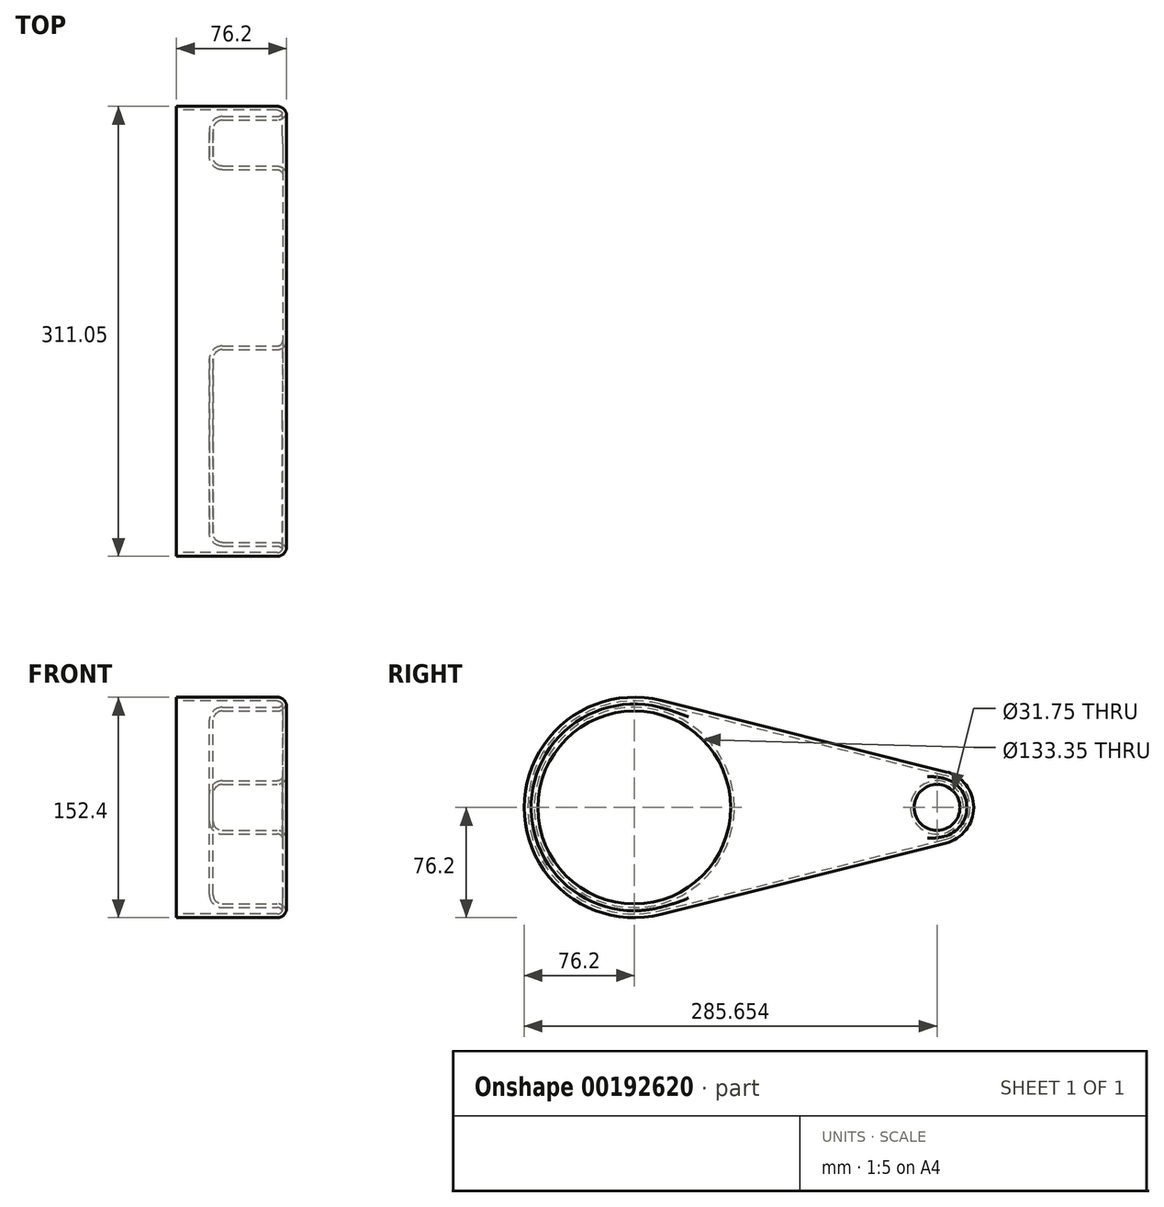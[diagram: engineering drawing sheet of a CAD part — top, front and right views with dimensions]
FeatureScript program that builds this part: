
annotation { "Feature Type Name" : "Feature", "Feature Type Description" : "" }
export const myFeature = defineFeature(function(context is Context, id is Id, definition is map)
    precondition{}
    {
        {
            var Q0;
            Q0=qCreatedBy(makeId("Right.planeOp"),FACE);
            var sketch = newSketch(context, id + "F0", { "sketchPlane" : qUnion([Q0])});
            skCircle(sketch, "E0", {"center": v(0, 0) * mm, "radius": 76.2 * mm});
            skCircle(sketch, "E1", {"center": v(209.45, 0) * mm, "radius": 25.4 * mm});
            skLineSegment(sketch, "E2", {"start": v(18.48, 73.92) * mm, "end": v(215.61, 24.64) * mm});
            skLineSegment(sketch, "E3", {"start": v(18.48, -73.92) * mm, "end": v(215.61, -24.64) * mm});
            skSolve(sketch);
        }
        {
            var Q0;
            {var subQ0=sQuery(id+"F0.wireOp",EDGE,"E0");var subQ1=makeQuery(id+"F0.imprint","INTERSECT",VERTEX,{"derivedFrom":[subQ0,sQuery(id+"F0.wireOp",EDGE,"E2")]});Q0=makeQuery(id+"F0.imprint","IMPRINT",FACE,{"disambiguationData":[TD([[makeQuery(id+"F0.imprint","IMPRINT",EDGE,{"disambiguationData":[TD([[subQ1,-1.0]])],"derivedFrom":subQ0}),1.0]])]});}
            var Q1;
            {var subQ0=sQuery(id+"F0.wireOp",EDGE,"E1");var subQ1=makeQuery(id+"F0.imprint","INTERSECT",VERTEX,{"derivedFrom":[subQ0,sQuery(id+"F0.wireOp",EDGE,"E2")]});Q1=makeQuery(id+"F0.imprint","IMPRINT",FACE,{"disambiguationData":[TD([[makeQuery(id+"F0.imprint","IMPRINT",EDGE,{"disambiguationData":[TD([[subQ1,-1.0]])],"derivedFrom":subQ0}),1.0]])]});}
            var Q2;
            {var subQ0=sQuery(id+"F0.wireOp",EDGE,"E2");Q2=makeQuery(id+"F0.imprint","IMPRINT",FACE,{"disambiguationData":[TD([[makeQuery(id+"F0.imprint","IMPRINT",EDGE,{"derivedFrom":subQ0}),-1.0]])]});}
            extrude(context, id + "F1", {"entities" : qUnion([Q0, Q1, Q2]), "depth" : 76.2 * mm});
        }
        {
            var Q0;
            Q0=makeQuery(id+"F1.opExtrude","CAP_FACE",FACE,{"disambiguationData":[OSD([sQuery(id+"F0.wireOp",EDGE,"E0"),sQuery(id+"F0.wireOp",EDGE,"E1"),sQuery(id+"F0.wireOp",EDGE,"E2"),sQuery(id+"F0.wireOp",EDGE,"E3")])],"isStart":false});
            var sketch = newSketch(context, id + "F2", { "sketchPlane" : qUnion([Q0])});
            skCircle(sketch, "E4", {"center": v(0, 0) * mm, "radius": 66.68 * mm});
            skCircle(sketch, "E5", {"center": v(209.45, 0) * mm, "radius": 15.88 * mm});
            skSolve(sketch);
        }
        {
            var Q0;
            Q0=makeQuery(id+"F2.imprint","IMPRINT",FACE,{"disambiguationData":[TD([[makeQuery(id+"F2.imprint","IMPRINT",EDGE,{"derivedFrom":sQuery(id+"F2.wireOp",EDGE,"E4")}),1.0]])]});
            var Q1;
            Q1=makeQuery(id+"F2.imprint","IMPRINT",FACE,{"disambiguationData":[TD([[makeQuery(id+"F2.imprint","IMPRINT",EDGE,{"derivedFrom":sQuery(id+"F2.wireOp",EDGE,"E5")}),1.0]])]});
            extrude(context, id + "F3", {"entities" : qUnion([Q0, Q1]), "operationType" : NewBodyOperationType.REMOVE, "oppositeDirection" : true, "depth" : 50.8 * mm});
        }
        {
            var Q0;
            Q0=makeQuery(id+"F1.opExtrude","CAP_FACE",FACE,{"disambiguationData":[OSD([sQuery(id+"F0.wireOp",EDGE,"E0"),sQuery(id+"F0.wireOp",EDGE,"E1"),sQuery(id+"F0.wireOp",EDGE,"E2"),sQuery(id+"F0.wireOp",EDGE,"E3")])],"isStart":false});
            var Q1;
            Q1=makeQuery(id+"F3.boolean.opBoolean","COPY",EDGE,{"derivedFrom":makeQuery(id+"F3.opExtrude","CAP_EDGE",EDGE,{"disambiguationData":[OSD([sQuery(id+"F2.wireOp",EDGE,"E4")])],"isStart":false})});
            var Q2;
            Q2=makeQuery(id+"F3.boolean.opBoolean","COPY",EDGE,{"derivedFrom":makeQuery(id+"F3.opExtrude","CAP_EDGE",EDGE,{"disambiguationData":[OSD([sQuery(id+"F2.wireOp",EDGE,"E5")])],"isStart":false})});
            fillet(context, id + "F4", {"entities" : qUnion([Q0, Q1, Q2]), "radius" : 6.35 * mm, "tangentPropagation" : true, "allowEdgeOverflow" : false});
        }
        {
            var Q0;
            Q0=makeQuery(id+"F1.opExtrude","CAP_FACE",FACE,{"disambiguationData":[OSD([sQuery(id+"F0.wireOp",EDGE,"E0"),sQuery(id+"F0.wireOp",EDGE,"E1"),sQuery(id+"F0.wireOp",EDGE,"E2"),sQuery(id+"F0.wireOp",EDGE,"E3")])],"isStart":true});
            shell(context, id + "F5", {"entities" : qUnion([Q0]), "thickness" : 2.54 * mm});
        }
    });
